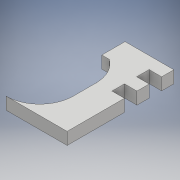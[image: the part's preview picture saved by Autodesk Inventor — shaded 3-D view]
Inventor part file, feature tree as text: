
AUTODESK INVENTOR PART (.ipt)
format: ipt  version: 2017 (Build 210142000, 142)  size: 127,488 bytes
history: native  units: mm
features: extrude x1, sketch x1
ambient origin geometry x8: Origin, YZ Plane, XZ Plane, XY Plane, X Axis, Y Axis, Z Axis, Center Point
bodies: Body1 (feature_tree)
feature tree (2):
  extrude  "Extrusion2"  TaperAngle=90.0deg  [1 undecoded]
  sketch  "Sketch1"  dims[d0=22.0mm d1=90.0deg d2=0.0mm d3=15.0mm d4=0.0mm d5=13.0mm d6=22.0mm d7=0.0mm d9=15.0mm d14=8.2mm d15=8.2mm d17=7.5mm d32=8.0mm d34=8.0mm d35=8.0mm d37=15.0mm d39=40.0mm d40=0.0mm d41=0.0mm d42=0.0mm d43=8.2mm d44=70.0mm d45=8.0mm d46=0.0mm]
note: 1 required parameter value undecoded (feature->parameter linkage not recoverable at this tier; creation-order binding heuristic only, values carry confidence <= 0.55)
